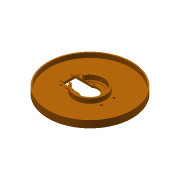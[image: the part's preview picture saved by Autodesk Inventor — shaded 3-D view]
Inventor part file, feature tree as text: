
AUTODESK INVENTOR PART (.ipt)
format: ipt  version: 2016 (Build 200138000, 138)  size: 209,920 bytes
history: native  units: mm
features: reference x36, sketch x7, extrude x6, other x1, hole x1, chamfer x1
ambient origin geometry x8: Origin, YZ Plane, XZ Plane, XY Plane, X Axis, Y Axis, Z Axis, Center Point
bodies: Solid1 (feature_tree)
feature tree (52):
  other  "skeleton.ipt"
  extrude  "Extrusion1"  Depth=58.0mm
  extrude  "Extrusion2"  Depth=15.0mm
  hole  "Hole1"  [1 undecoded]
  extrude  "Extrusion6"  Depth=10.0mm
  chamfer  "Chamfer1"  Distance=1.0mm
  extrude  "Extrusion7"  Depth=10.0mm
  extrude  "Extrusion8"  Depth=3.0mm
  extrude  "Extrusion9"  Depth=24.0mm
  sketch  "Sketch1"  dims[d0=1.0mm d1=58.0mm]
  reference  "Reference1"
  reference  "Reference2"
  reference  "Reference3"
  reference  "Reference4"
  reference  "Reference5"
  reference  "Reference6"
  reference  "Reference7"
  reference  "Reference8"
  reference  "Reference9"
  reference  "Reference10"
  reference  "Reference11"
  reference  "Reference12"
  reference  "Reference13"
  reference  "Reference14"
  reference  "Reference15"
  reference  "Reference16"
  reference  "Reference17"
  reference  "Reference18"
  reference  "Reference19"
  reference  "Reference20"
  sketch  "Sketch2"  dims[d2=38.0mm d3=15.0mm]
  reference  "Reference21"
  reference  "Reference22"
  reference  "Reference23"
  reference  "Reference24"
  sketch  "Sketch3"  dims[d4=4.0mm d5=0.0mm d6=3.0mm d7=0.0mm]
  reference  "Reference25"
  reference  "Reference26"
  reference  "Reference27"
  reference  "Reference28"
  reference  "Reference29"
  reference  "Reference30"
  reference  "Reference31"
  reference  "Reference32"
  reference  "Reference33"
  reference  "Reference34"
  sketch  "Sketch7"  dims[d8=2.2mm d9=6.0mm d10=4.0mm d11=2.0mm d12=90.0deg d13=8.0mm d14=20.594885mm d27=10.0mm]
  sketch  "Sketch8"  dims[d28=120.0mm]
  sketch  "Sketch9"  dims[d29=36.0mm d30=1.0mm d31=0.0mm]
  sketch  "Sketch10"  dims[d32=1.0mm d33=2.0mm d34=45.0deg d35=42.0mm d36=3.0mm d37=24.0mm d38=21.0mm d39=21.0mm d40=21.0mm d41=7.0mm d42=0.0mm d43=2.0mm d44=7.0mm d45=0.0mm d46=10.0mm d47=0.0mm]
  reference  "Reference39"
  reference  "Reference40"
note: 1 required parameter value undecoded (feature->parameter linkage not recoverable at this tier; creation-order binding heuristic only, values carry confidence <= 0.55)
